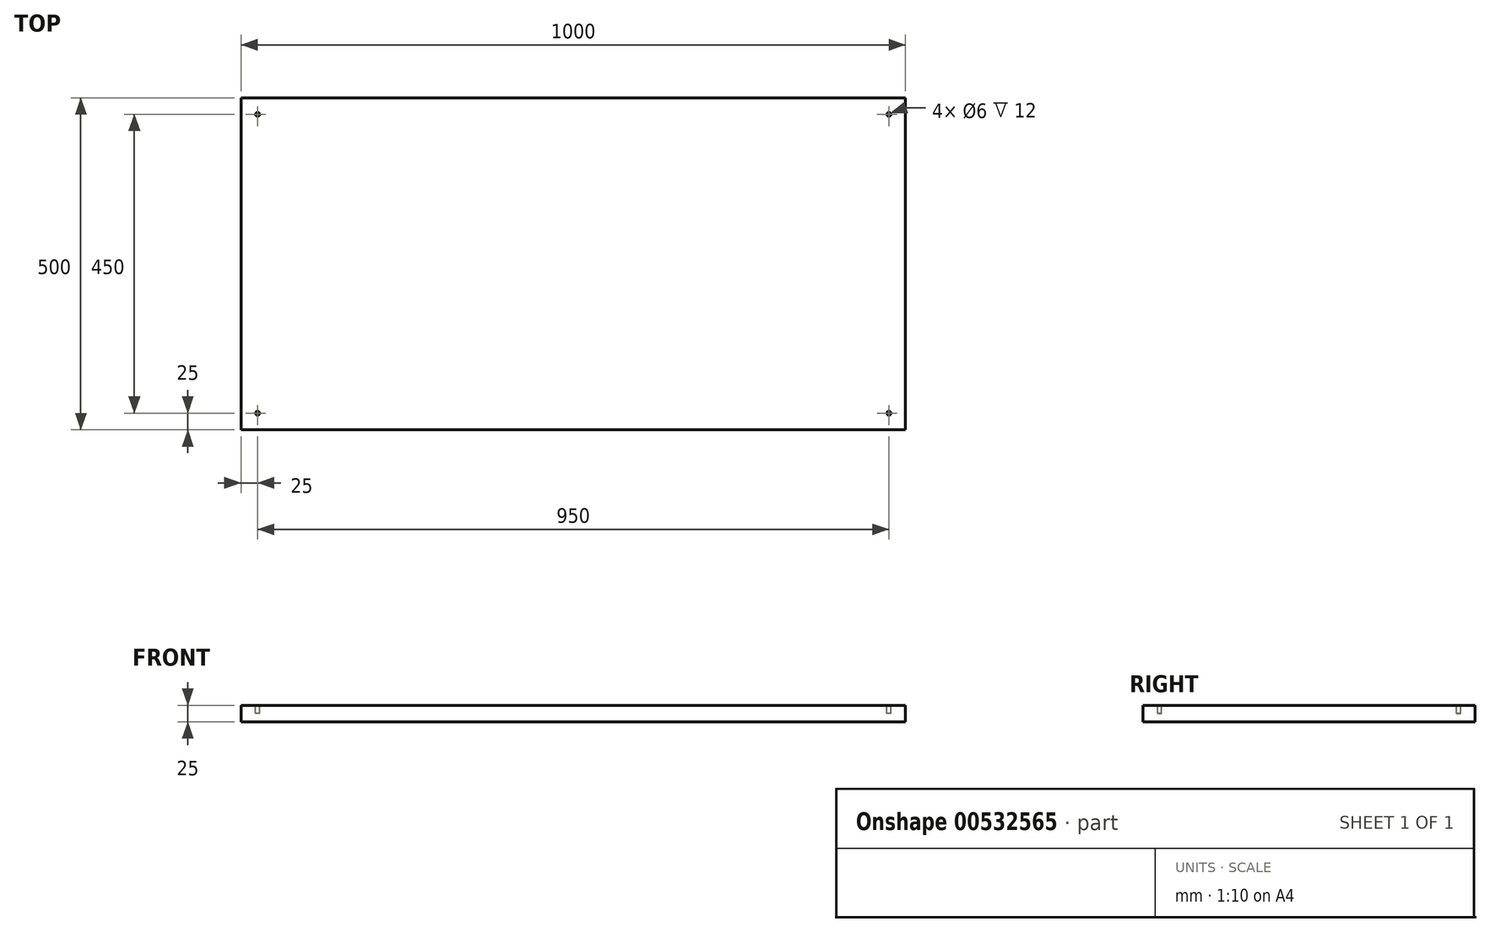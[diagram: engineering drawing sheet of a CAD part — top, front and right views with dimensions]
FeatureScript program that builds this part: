
annotation { "Feature Type Name" : "Feature", "Feature Type Description" : "" }
export const myFeature = defineFeature(function(context is Context, id is Id, definition is map)
    precondition{}
    {
        {
            var Q0;
            Q0=qCreatedBy(makeId("Top.planeOp"),FACE);
            var sketch = newSketch(context, id + "F0", { "sketchPlane" : qUnion([Q0])});
            skLineSegment(sketch, "E0.bottom", {"start": v(0, 0) * mm, "end": v(1000, 0) * mm});
            skLineSegment(sketch, "E0.top", {"start": v(0, 500) * mm, "end": v(1000, 500) * mm});
            skLineSegment(sketch, "E0.left", {"start": v(0, 0) * mm, "end": v(0, 500) * mm});
            skLineSegment(sketch, "E0.right", {"start": v(1000, 0) * mm, "end": v(1000, 500) * mm});
            skSolve(sketch);
        }
        {
            var Q0;
            Q0 = qSketchRegion(id + "F0", true);
            extrude(context, id + "F1", {"entities" : qUnion([Q0]), "depth" : 25 * mm, "offsetDistance" : 25 * mm});
        }
        {
            var Q0;
            Q0=makeQuery(id+"F1.opExtrude","CAP_FACE",FACE,{"disambiguationData":[OSD([sQuery(id+"F0.wireOp",EDGE,"E0.bottom"),sQuery(id+"F0.wireOp",EDGE,"E0.top"),sQuery(id+"F0.wireOp",EDGE,"E0.left"),sQuery(id+"F0.wireOp",EDGE,"E0.right")])],"isStart":false});
            var sketch = newSketch(context, id + "F2", { "sketchPlane" : qUnion([Q0])});
            skLineSegment(sketch, "E1.bottom", {"start": v(0, 500) * mm, "end": v(50, 500) * mm});
            skLineSegment(sketch, "E1.top", {"start": v(0, 450) * mm, "end": v(50, 450) * mm});
            skLineSegment(sketch, "E1.left", {"start": v(0, 500) * mm, "end": v(0, 450) * mm});
            skLineSegment(sketch, "E1.right", {"start": v(50, 500) * mm, "end": v(50, 450) * mm});
            skLineSegment(sketch, "E2.bottom", {"start": v(0, 0) * mm, "end": v(50, 0) * mm});
            skLineSegment(sketch, "E2.top", {"start": v(0, 50) * mm, "end": v(50, 50) * mm});
            skLineSegment(sketch, "E2.left", {"start": v(0, 0) * mm, "end": v(0, 50) * mm});
            skLineSegment(sketch, "E2.right", {"start": v(50, 0) * mm, "end": v(50, 50) * mm});
            skSolve(sketch);
        }
        {
            var Q0;
            Q0 = qSketchRegion(id + "F2", true);
            extrude(context, id + "F3", {"entities" : qUnion([Q0]), "operationType" : NewBodyOperationType.ADD, "oppositeDirection" : true, "depth" : 24 * mm, "offsetDistance" : 25 * mm});
        }
        {
            var Q0;
            Q0=makeQuery(id+"F1.opExtrude","CAP_FACE",FACE,{"disambiguationData":[OSD([sQuery(id+"F0.wireOp",EDGE,"E0.bottom"),sQuery(id+"F0.wireOp",EDGE,"E0.top"),sQuery(id+"F0.wireOp",EDGE,"E0.left"),sQuery(id+"F0.wireOp",EDGE,"E0.right")])],"isStart":false});
            var sketch = newSketch(context, id + "F4", { "sketchPlane" : qUnion([Q0])});
            skCircle(sketch, "E3", {"center": v(975, 475) * mm, "radius": 3 * mm});
            skCircle(sketch, "E4", {"center": v(975, 25) * mm, "radius": 3 * mm});
            skSolve(sketch);
        }
        {
            var Q0;
            Q0 = qSketchRegion(id + "F4", true);
            extrude(context, id + "F5", {"entities" : qUnion([Q0]), "operationType" : NewBodyOperationType.REMOVE, "oppositeDirection" : true, "depth" : 12 * mm, "offsetDistance" : 25 * mm});
        }
        {
            var Q0;
            Q0=makeQuery(id+"F1.opExtrude","CAP_FACE",FACE,{"disambiguationData":[OSD([sQuery(id+"F0.wireOp",EDGE,"E0.bottom"),sQuery(id+"F0.wireOp",EDGE,"E0.top"),sQuery(id+"F0.wireOp",EDGE,"E0.left"),sQuery(id+"F0.wireOp",EDGE,"E0.right")])],"isStart":false});
            var sketch = newSketch(context, id + "F6", { "sketchPlane" : qUnion([Q0])});
            skCircle(sketch, "E5", {"center": v(25, 475) * mm, "radius": 3 * mm});
            skCircle(sketch, "E6", {"center": v(25, 25) * mm, "radius": 3 * mm});
            skSolve(sketch);
        }
        {
            var Q0;
            Q0 = qSketchRegion(id + "F6", true);
            extrude(context, id + "F7", {"entities" : qUnion([Q0]), "operationType" : NewBodyOperationType.REMOVE, "oppositeDirection" : true, "depth" : 12 * mm, "offsetDistance" : 25 * mm});
        }
    });
